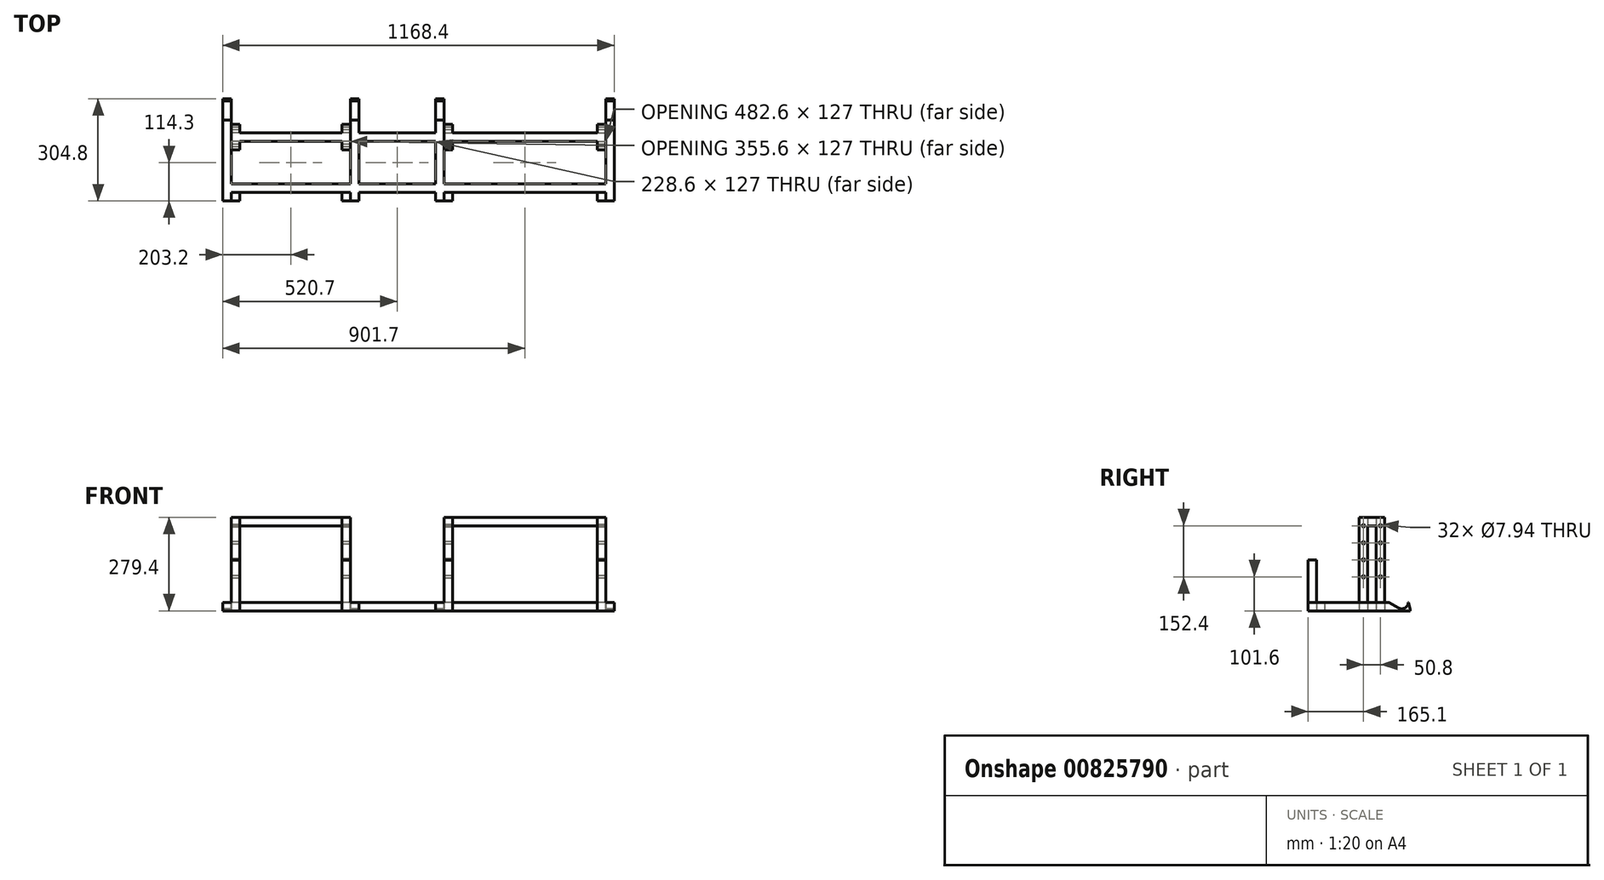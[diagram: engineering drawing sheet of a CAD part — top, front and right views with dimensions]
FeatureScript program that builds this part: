
annotation { "Feature Type Name" : "Feature", "Feature Type Description" : "" }
export const myFeature = defineFeature(function(context is Context, id is Id, definition is map)
    precondition{}
    {
        {
            var Q0;
            Q0=qCreatedBy(makeId("Right.planeOp"),FACE);
            var sketch = newSketch(context, id + "F0", { "sketchPlane" : qUnion([Q0])});
            skLineSegment(sketch, "E0.bottom", {"start": v(0, 0) * mm, "end": v(25.4, 0) * mm});
            skLineSegment(sketch, "E0.top", {"start": v(0, 25.4) * mm, "end": v(25.4, 25.4) * mm});
            skLineSegment(sketch, "E0.left", {"start": v(0, 0) * mm, "end": v(0, 25.4) * mm});
            skLineSegment(sketch, "E0.right", {"start": v(25.4, 0) * mm, "end": v(25.4, 25.4) * mm});
            skLineSegment(sketch, "E1.bottom", {"start": v(177.8, 0) * mm, "end": v(152.4, 0) * mm});
            skLineSegment(sketch, "E1.top", {"start": v(177.8, 25.4) * mm, "end": v(152.4, 25.4) * mm});
            skLineSegment(sketch, "E1.left", {"start": v(177.8, 0) * mm, "end": v(177.8, 25.4) * mm});
            skLineSegment(sketch, "E1.right", {"start": v(152.4, 0) * mm, "end": v(152.4, 25.4) * mm});
            skSolve(sketch);
        }
        {
            var Q0;
            Q0 = qSketchRegion(id + "F0", true);
            extrude(context, id + "F1", {"entities" : qUnion([Q0]), "endBound" : BoundingType.SYMMETRIC, "depth" : 1168.4 * mm, "offsetDistance" : 25.4 * mm});
        }
        {
            var Q0;
            Q0=qCreatedBy(makeId("Front.planeOp"),FACE);
            var sketch = newSketch(context, id + "F2", { "sketchPlane" : qUnion([Q0])});
            skLineSegment(sketch, "E2.bottom", {"start": v(-584.2, 0) * mm, "end": v(-558.8, 0) * mm});
            skLineSegment(sketch, "E2.top", {"start": v(-584.2, 25.4) * mm, "end": v(-558.8, 25.4) * mm});
            skLineSegment(sketch, "E2.left", {"start": v(-584.2, 0) * mm, "end": v(-584.2, 25.4) * mm});
            skLineSegment(sketch, "E2.right", {"start": v(-558.8, 0) * mm, "end": v(-558.8, 25.4) * mm});
            skLineSegment(sketch, "E3.bottom", {"start": v(-203.2, 0) * mm, "end": v(-177.8, 0) * mm});
            skLineSegment(sketch, "E3.top", {"start": v(-203.2, 25.4) * mm, "end": v(-177.8, 25.4) * mm});
            skLineSegment(sketch, "E3.left", {"start": v(-203.2, 0) * mm, "end": v(-203.2, 25.4) * mm});
            skLineSegment(sketch, "E3.right", {"start": v(-177.8, 0) * mm, "end": v(-177.8, 25.4) * mm});
            skLineSegment(sketch, "E4.bottom", {"start": v(50.8, 0) * mm, "end": v(76.2, 0) * mm});
            skLineSegment(sketch, "E4.top", {"start": v(50.8, 25.4) * mm, "end": v(76.2, 25.4) * mm});
            skLineSegment(sketch, "E4.left", {"start": v(50.8, 0) * mm, "end": v(50.8, 25.4) * mm});
            skLineSegment(sketch, "E4.right", {"start": v(76.2, 0) * mm, "end": v(76.2, 25.4) * mm});
            skLineSegment(sketch, "E5.bottom", {"start": v(558.8, 0) * mm, "end": v(584.2, 0) * mm});
            skLineSegment(sketch, "E5.top", {"start": v(558.8, 25.4) * mm, "end": v(584.2, 25.4) * mm});
            skLineSegment(sketch, "E5.left", {"start": v(558.8, 0) * mm, "end": v(558.8, 25.4) * mm});
            skLineSegment(sketch, "E5.right", {"start": v(584.2, 0) * mm, "end": v(584.2, 25.4) * mm});
            skSolve(sketch);
        }
        {
            var Q0;
            Q0 = qSketchRegion(id + "F2", true);
            var Q1;
            Q1=makeQuery(id+"F1.opExtrude","SWEPT_FACE",FACE,{"disambiguationData":[OSD([sQuery(id+"F0.wireOp",EDGE,"E1.left")])]});
            extrude(context, id + "F3", {"entities" : qUnion([Q0]), "operationType" : NewBodyOperationType.ADD, "endBound" : BoundingType.UP_TO_SURFACE, "oppositeDirection" : true, "depth" : 254 * mm, "endBoundEntityFace" : qUnion([Q1]), "hasOffset" : true, "offsetDistance" : 101.6 * mm, "offsetOppositeDirection" : true, "hasSecondDirection" : true, "secondDirectionOppositeDirection" : false, "secondDirectionDepth" : 25.4 * mm});
        }
        {
            var Q0;
            Q0=qCreatedBy(makeId("Right.planeOp"),FACE);
            var sketch = newSketch(context, id + "F4", { "sketchPlane" : qUnion([Q0])});
            skArc(sketch, "E6", {"start": v(244.47, 8.9) * mm, "mid": v(272.4, 20.47) * mm, "end": v(254, 44.45) * mm});
            skLineSegment(sketch, "E7", {"start": v(244.47, 8.9) * mm, "end": v(215.9, 25.4) * mm});
            skLineSegment(sketch, "E8", {"start": v(215.9, 25.4) * mm, "end": v(215.9, 44.45) * mm});
            skLineSegment(sketch, "E9", {"start": v(215.9, 44.45) * mm, "end": v(254, 44.45) * mm});
            skLineSegment(sketch, "E10", {"start": v(279.4, 25.4) * mm, "end": v(273.69, 25.4) * mm});
            skLineSegment(sketch, "E11", {"start": v(273.68, 25.4) * mm, "end": v(279.4, 4.07) * mm});
            skLineSegment(sketch, "E12", {"start": v(279.4, 4.07) * mm, "end": v(279.4, 25.4) * mm});
            skSolve(sketch);
        }
        {
            var Q0;
            Q0 = qSketchRegion(id + "F4", true);
            extrude(context, id + "F5", {"entities" : qUnion([Q0]), "operationType" : NewBodyOperationType.REMOVE, "endBound" : BoundingType.THROUGH_ALL, "depth" : 25.4 * mm, "offsetDistance" : 25.4 * mm, "hasSecondDirection" : true, "secondDirectionBound" : SecondDirectionBoundingType.THROUGH_ALL, "secondDirectionOppositeDirection" : true, "secondDirectionDepth" : 25.4 * mm});
        }
        {
            var Q0;
            Q0=qCreatedBy(makeId("Top.planeOp"),FACE);
            var sketch = newSketch(context, id + "F6", { "sketchPlane" : qUnion([Q0])});
            skLineSegment(sketch, "E13.bottom", {"start": v(-558.8, 177.8) * mm, "end": v(-533.4, 177.8) * mm});
            skLineSegment(sketch, "E13.top", {"start": v(-558.8, 203.2) * mm, "end": v(-533.4, 203.2) * mm});
            skLineSegment(sketch, "E13.left", {"start": v(-558.8, 177.8) * mm, "end": v(-558.8, 203.2) * mm});
            skLineSegment(sketch, "E13.right", {"start": v(-533.4, 177.8) * mm, "end": v(-533.4, 203.2) * mm});
            skLineSegment(sketch, "E14.bottom", {"start": v(-558.8, 152.4) * mm, "end": v(-533.4, 152.4) * mm});
            skLineSegment(sketch, "E14.top", {"start": v(-558.8, 127) * mm, "end": v(-533.4, 127) * mm});
            skLineSegment(sketch, "E14.left", {"start": v(-558.8, 152.4) * mm, "end": v(-558.8, 127) * mm});
            skLineSegment(sketch, "E14.right", {"start": v(-533.4, 152.4) * mm, "end": v(-533.4, 127) * mm});
            skLineSegment(sketch, "E15.bottom", {"start": v(-228.6, 127) * mm, "end": v(-203.2, 127) * mm});
            skLineSegment(sketch, "E15.top", {"start": v(-228.6, 152.4) * mm, "end": v(-203.2, 152.4) * mm});
            skLineSegment(sketch, "E15.left", {"start": v(-228.6, 127) * mm, "end": v(-228.6, 152.4) * mm});
            skLineSegment(sketch, "E15.right", {"start": v(-203.2, 127) * mm, "end": v(-203.2, 152.4) * mm});
            skLineSegment(sketch, "E16.bottom", {"start": v(-228.6, 203.2) * mm, "end": v(-203.2, 203.2) * mm});
            skLineSegment(sketch, "E16.top", {"start": v(-228.6, 177.8) * mm, "end": v(-203.2, 177.8) * mm});
            skLineSegment(sketch, "E16.left", {"start": v(-228.6, 203.2) * mm, "end": v(-228.6, 177.8) * mm});
            skLineSegment(sketch, "E16.right", {"start": v(-203.2, 203.2) * mm, "end": v(-203.2, 177.8) * mm});
            skLineSegment(sketch, "E17.bottom", {"start": v(76.2, 203.2) * mm, "end": v(101.6, 203.2) * mm});
            skLineSegment(sketch, "E17.top", {"start": v(76.2, 177.8) * mm, "end": v(101.6, 177.8) * mm});
            skLineSegment(sketch, "E17.left", {"start": v(76.2, 203.2) * mm, "end": v(76.2, 177.8) * mm});
            skLineSegment(sketch, "E17.right", {"start": v(101.6, 203.2) * mm, "end": v(101.6, 177.8) * mm});
            skLineSegment(sketch, "E18.bottom", {"start": v(533.4, 203.2) * mm, "end": v(558.8, 203.2) * mm});
            skLineSegment(sketch, "E18.top", {"start": v(533.4, 177.8) * mm, "end": v(558.8, 177.8) * mm});
            skLineSegment(sketch, "E18.left", {"start": v(533.4, 203.2) * mm, "end": v(533.4, 177.8) * mm});
            skLineSegment(sketch, "E18.right", {"start": v(558.8, 203.2) * mm, "end": v(558.8, 177.8) * mm});
            skLineSegment(sketch, "E19.bottom", {"start": v(533.4, 152.4) * mm, "end": v(558.8, 152.4) * mm});
            skLineSegment(sketch, "E19.top", {"start": v(533.4, 127) * mm, "end": v(558.8, 127) * mm});
            skLineSegment(sketch, "E19.left", {"start": v(533.4, 152.4) * mm, "end": v(533.4, 127) * mm});
            skLineSegment(sketch, "E19.right", {"start": v(558.8, 152.4) * mm, "end": v(558.8, 127) * mm});
            skLineSegment(sketch, "E20.bottom", {"start": v(76.2, 127) * mm, "end": v(101.6, 127) * mm});
            skLineSegment(sketch, "E20.top", {"start": v(76.2, 152.4) * mm, "end": v(101.6, 152.4) * mm});
            skLineSegment(sketch, "E20.left", {"start": v(76.2, 127) * mm, "end": v(76.2, 152.4) * mm});
            skLineSegment(sketch, "E20.right", {"start": v(101.6, 127) * mm, "end": v(101.6, 152.4) * mm});
            skSolve(sketch);
        }
        {
            var Q0;
            Q0 = qSketchRegion(id + "F6", true);
            extrude(context, id + "F7", {"entities" : qUnion([Q0]), "operationType" : NewBodyOperationType.ADD, "depth" : 279.4 * mm, "offsetDistance" : 25.4 * mm});
        }
        {
            var Q0;
            Q0=makeQuery(id+"F7.opExtrude","SWEPT_FACE",FACE,{"disambiguationData":[OSD([sQuery(id+"F6.wireOp",EDGE,"E14.left")])]});
            var sketch = newSketch(context, id + "F8", { "sketchPlane" : qUnion([Q0])});
            skLineSegment(sketch, "E21.bottom", {"start": v(-177.8, 279.4) * mm, "end": v(-152.4, 279.4) * mm});
            skLineSegment(sketch, "E21.top", {"start": v(-177.8, 254) * mm, "end": v(-152.4, 254) * mm});
            skLineSegment(sketch, "E21.left", {"start": v(-177.8, 279.4) * mm, "end": v(-177.8, 254) * mm});
            skLineSegment(sketch, "E21.right", {"start": v(-152.4, 279.4) * mm, "end": v(-152.4, 254) * mm});
            skSolve(sketch);
        }
        {
            var Q0;
            Q0 = qSketchRegion(id + "F8", true);
            var Q1;
            Q1=makeQuery(id+"F7.opExtrude","SWEPT_FACE",FACE,{"disambiguationData":[OSD([sQuery(id+"F6.wireOp",EDGE,"E16.right")])]});
            extrude(context, id + "F9", {"entities" : qUnion([Q0]), "operationType" : NewBodyOperationType.ADD, "endBound" : BoundingType.UP_TO_SURFACE, "oppositeDirection" : true, "depth" : 25.4 * mm, "endBoundEntityFace" : qUnion([Q1]), "offsetDistance" : 25.4 * mm});
        }
        {
            var Q0;
            Q0=makeQuery(id+"F7.opExtrude","SWEPT_FACE",FACE,{"disambiguationData":[OSD([sQuery(id+"F6.wireOp",EDGE,"E18.right")])]});
            var sketch = newSketch(context, id + "F10", { "sketchPlane" : qUnion([Q0])});
            skLineSegment(sketch, "E22.bottom", {"start": v(152.4, 279.4) * mm, "end": v(177.8, 279.4) * mm});
            skLineSegment(sketch, "E22.top", {"start": v(152.4, 254) * mm, "end": v(177.8, 254) * mm});
            skLineSegment(sketch, "E22.left", {"start": v(152.4, 279.4) * mm, "end": v(152.4, 254) * mm});
            skLineSegment(sketch, "E22.right", {"start": v(177.8, 279.4) * mm, "end": v(177.8, 254) * mm});
            skSolve(sketch);
        }
        {
            var Q0;
            Q0 = qSketchRegion(id + "F10", true);
            var Q1;
            Q1=makeQuery(id+"F7.opExtrude","SWEPT_FACE",FACE,{"disambiguationData":[OSD([sQuery(id+"F6.wireOp",EDGE,"E20.left")])]});
            extrude(context, id + "F11", {"entities" : qUnion([Q0]), "operationType" : NewBodyOperationType.ADD, "endBound" : BoundingType.UP_TO_SURFACE, "oppositeDirection" : true, "depth" : 25.4 * mm, "endBoundEntityFace" : qUnion([Q1]), "offsetDistance" : 25.4 * mm});
        }
        {
            var Q0;
            Q0=makeQuery(id+"F9.boolean.opBoolean","MERGE",FACE,{"derivedFrom":[makeQuery(id+"F7.opExtrude","SWEPT_FACE",FACE,{"disambiguationData":[OSD([sQuery(id+"F6.wireOp",EDGE,"E13.left")])]}),makeQuery(id+"F7.opExtrude","SWEPT_FACE",FACE,{"disambiguationData":[OSD([sQuery(id+"F6.wireOp",EDGE,"E14.left")])]}),makeQuery(id+"F9.opExtrude","CAP_FACE",FACE,{"disambiguationData":[OSD([sQuery(id+"F8.wireOp",EDGE,"E21.bottom"),sQuery(id+"F8.wireOp",EDGE,"E21.top"),sQuery(id+"F8.wireOp",EDGE,"E21.left"),sQuery(id+"F8.wireOp",EDGE,"E21.right")])],"isStart":true})]});
            var sketch = newSketch(context, id + "F12", { "sketchPlane" : qUnion([Q0])});
            skCircle(sketch, "E23", {"center": v(-139.7, 101.6) * mm, "radius": 3.97 * mm});
            skLineSegment(sketch, "E24", {"start": v(-152.4, 101.6) * mm, "end": v(-127, 101.6) * mm, "construction": true});
            skCircle(sketch, "E25.0.1.0", {"center": v(-139.7, 152.4) * mm, "radius": 3.97 * mm});
            skCircle(sketch, "E25.0.2.0", {"center": v(-139.7, 203.2) * mm, "radius": 3.97 * mm});
            skCircle(sketch, "E25.0.3.0", {"center": v(-139.7, 254) * mm, "radius": 3.97 * mm});
            skCircle(sketch, "E25.1.0.0", {"center": v(-190.5, 101.6) * mm, "radius": 3.97 * mm});
            skCircle(sketch, "E25.1.1.0", {"center": v(-190.5, 152.4) * mm, "radius": 3.97 * mm});
            skCircle(sketch, "E25.1.2.0", {"center": v(-190.5, 203.2) * mm, "radius": 3.97 * mm});
            skCircle(sketch, "E25.1.3.0", {"center": v(-190.5, 254) * mm, "radius": 3.97 * mm});
            skLineSegment(sketch, "E25.direction1", {"start": v(-139.7, 101.6) * mm, "end": v(-190.5, 101.6) * mm, "construction": true});
            skLineSegment(sketch, "E25.direction2", {"start": v(-139.7, 101.6) * mm, "end": v(-139.7, 152.4) * mm, "construction": true});
            skSolve(sketch);
        }
        {
            var Q0;
            Q0 = qSketchRegion(id + "F12", true);
            extrude(context, id + "F13", {"entities" : qUnion([Q0]), "operationType" : NewBodyOperationType.REMOVE, "endBound" : BoundingType.THROUGH_ALL, "oppositeDirection" : true, "depth" : 25.4 * mm, "offsetDistance" : 25.4 * mm});
        }
        {
            var Q0;
            Q0=qCreatedBy(makeId("Top.planeOp"),FACE);
            var sketch = newSketch(context, id + "F14", { "sketchPlane" : qUnion([Q0])});
            skLineSegment(sketch, "E26.bottom", {"start": v(-558.8, -25.4) * mm, "end": v(-533.4, -25.4) * mm});
            skLineSegment(sketch, "E26.top", {"start": v(-558.8, 0) * mm, "end": v(-533.4, 0) * mm});
            skLineSegment(sketch, "E26.left", {"start": v(-558.8, -25.4) * mm, "end": v(-558.8, 0) * mm});
            skLineSegment(sketch, "E26.right", {"start": v(-533.4, -25.4) * mm, "end": v(-533.4, 0) * mm});
            skLineSegment(sketch, "E27.bottom", {"start": v(-203.2, -25.4) * mm, "end": v(-228.6, -25.4) * mm});
            skLineSegment(sketch, "E27.top", {"start": v(-203.2, 0) * mm, "end": v(-228.6, 0) * mm});
            skLineSegment(sketch, "E27.left", {"start": v(-203.2, -25.4) * mm, "end": v(-203.2, 0) * mm});
            skLineSegment(sketch, "E27.right", {"start": v(-228.6, -25.4) * mm, "end": v(-228.6, 0) * mm});
            skLineSegment(sketch, "E28.bottom", {"start": v(76.2, -25.4) * mm, "end": v(101.6, -25.4) * mm});
            skLineSegment(sketch, "E28.top", {"start": v(76.2, 0) * mm, "end": v(101.6, 0) * mm});
            skLineSegment(sketch, "E28.left", {"start": v(76.2, -25.4) * mm, "end": v(76.2, 0) * mm});
            skLineSegment(sketch, "E28.right", {"start": v(101.6, -25.4) * mm, "end": v(101.6, 0) * mm});
            skLineSegment(sketch, "E29.bottom", {"start": v(533.4, -25.4) * mm, "end": v(558.8, -25.4) * mm});
            skLineSegment(sketch, "E29.top", {"start": v(533.4, 0) * mm, "end": v(558.8, 0) * mm});
            skLineSegment(sketch, "E29.left", {"start": v(533.4, -25.4) * mm, "end": v(533.4, 0) * mm});
            skLineSegment(sketch, "E29.right", {"start": v(558.8, -25.4) * mm, "end": v(558.8, 0) * mm});
            skSolve(sketch);
        }
        {
            var Q0;
            Q0 = qSketchRegion(id + "F14", true);
            extrude(context, id + "F15", {"entities" : qUnion([Q0]), "operationType" : NewBodyOperationType.ADD, "depth" : 152.4 * mm, "offsetDistance" : 25.4 * mm});
        }
    });
